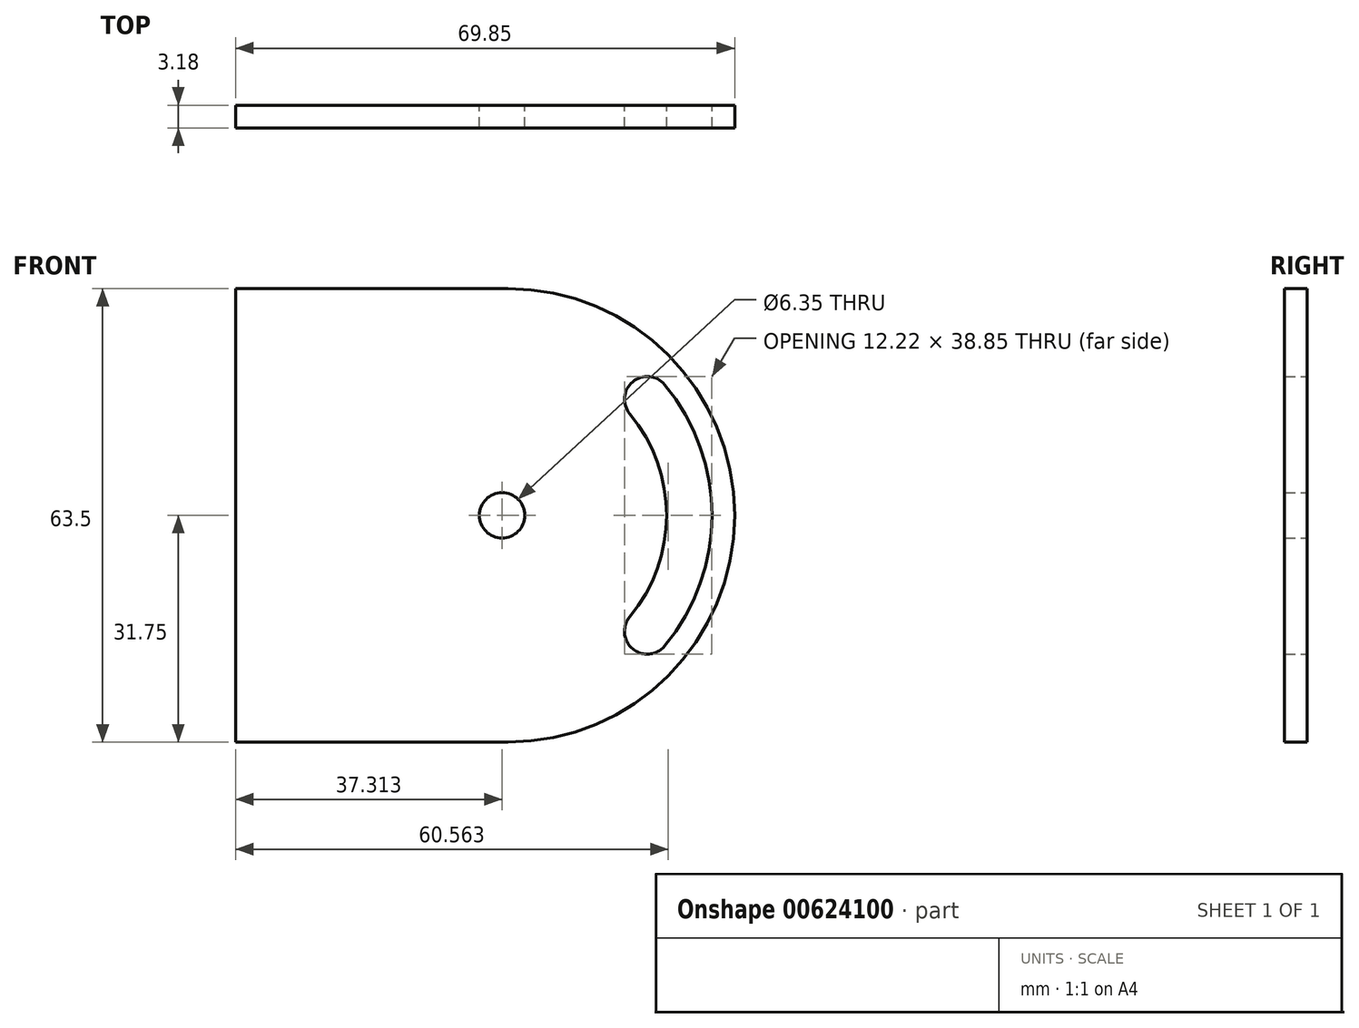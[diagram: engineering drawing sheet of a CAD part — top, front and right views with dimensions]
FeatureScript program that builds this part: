
annotation { "Feature Type Name" : "Feature", "Feature Type Description" : "" }
export const myFeature = defineFeature(function(context is Context, id is Id, definition is map)
    precondition{}
    {
        {
            var Q0;
            Q0=qCreatedBy(makeId("Front.planeOp"),FACE);
            var sketch = newSketch(context, id + "F0", { "sketchPlane" : qUnion([Q0])});
            skLineSegment(sketch, "E0.bottom", {"start": v(0, 0) * mm, "end": v(38.1, 0) * mm});
            skLineSegment(sketch, "E0.top", {"start": v(0, 63.5) * mm, "end": v(38.1, 63.5) * mm});
            skLineSegment(sketch, "E0.left", {"start": v(0, 0) * mm, "end": v(0, 63.5) * mm});
            skLineSegment(sketch, "E0.right", {"start": v(69.85, 31.75) * mm, "end": v(69.85, 31.75) * mm});
            skCircle(sketch, "E1", {"center": v(38.1, 31.75) * mm, "radius": 28.58 * mm});
            skCircle(sketch, "E2", {"center": v(38.1, 31.75) * mm, "radius": 22.23 * mm});
            skLineSegment(sketch, "E3", {"start": v(55.17, 45.98) * mm, "end": v(60.05, 50.04) * mm});
            skLineSegment(sketch, "E4", {"start": v(55.17, 17.52) * mm, "end": v(60.05, 13.46) * mm});
            skCircle(sketch, "E5", {"center": v(57.61, 15.49) * mm, "radius": 3.18 * mm});
            skCircle(sketch, "E6", {"center": v(57.61, 48.01) * mm, "radius": 3.18 * mm});
            skPoint(sketch, "E7.visualSharp", {"position": v(69.85, 63.5) * mm});
            skArc(sketch, "E7.filletArc", {"start": v(69.85, 31.75) * mm, "mid": v(60.55, 54.2) * mm, "end": v(38.1, 63.5) * mm});
            skPoint(sketch, "E8.visualSharp", {"position": v(69.85, 0) * mm});
            skArc(sketch, "E8.filletArc", {"start": v(38.1, 0) * mm, "mid": v(60.55, 9.3) * mm, "end": v(69.85, 31.75) * mm});
            skLineSegment(sketch, "E9", {"start": v(38.1, 31.75) * mm, "end": v(69.85, 31.75) * mm});
            skLineSegment(sketch, "E10", {"start": v(38.1, 31.75) * mm, "end": v(38.1, 31.75) * mm});
            skSolve(sketch);
        }
        {
            var Q0;
            {var subQ0=sQuery(id+"F0.wireOp",EDGE,"E6");var subQ1=sQuery(id+"F0.wireOp",EDGE,"E3");var subQ2=sQuery(id+"F0.wireOp",EDGE,"E1");var subQ3=makeQuery(id+"F0.imprint","INTERSECT",VERTEX,{"derivedFrom":[subQ2,subQ1,subQ0]});Q0=makeQuery(id+"F0.imprint","IMPRINT",FACE,{"disambiguationData":[TD([[makeQuery(id+"F0.imprint","IMPRINT",EDGE,{"disambiguationData":[TD([[subQ3,-1.0]])],"derivedFrom":subQ2}),1.0]])]});}
            var Q1;
            Q1=makeQuery(id+"F0.imprint","IMPRINT",FACE,{"disambiguationData":[TD([[makeQuery(id+"F0.imprint","IMPRINT",EDGE,{"derivedFrom":sQuery(id+"F0.wireOp",EDGE,"E0.bottom")}),1.0]])]});
            var Q2;
            Q2=makeQuery(id+"F0.imprint","IMPRINT",FACE,{"disambiguationData":[TD([[makeQuery(id+"F0.imprint","IMPRINT",EDGE,{"derivedFrom":sQuery(id+"F0.wireOp",EDGE,"WlHfUtpb-D6SS-SN8B-bFR3-Eu7baDn13T6m")}),-1.0]])]});
            var Q3;
            {var subQ0=sQuery(id+"F0.wireOp",EDGE,"E2");var subQ1=makeQuery(id+"F0.imprint","INTERSECT",VERTEX,{"derivedFrom":[subQ0,sQuery(id+"F0.wireOp",EDGE,"E3"),sQuery(id+"F0.wireOp",EDGE,"E6")]});Q3=makeQuery(id+"F0.imprint","IMPRINT",FACE,{"disambiguationData":[TD([[makeQuery(id+"F0.imprint","IMPRINT",EDGE,{"disambiguationData":[TD([[subQ1,-1.0]])],"derivedFrom":subQ0}),1.0]])]});}
            extrude(context, id + "F1", {"entities" : qUnion([Q0, Q1, Q2, Q3]), "depth" : 3.17 * mm, "offsetDistance" : 25.4 * mm});
        }
        {
            var Q0;
            Q0=makeQuery(id+"F1.opExtrude","CAP_FACE",FACE,{"disambiguationData":[OSD([sQuery(id+"F0.wireOp",EDGE,"E0.bottom"),sQuery(id+"F0.wireOp",EDGE,"E0.top"),sQuery(id+"F0.wireOp",EDGE,"E0.left"),sQuery(id+"F0.wireOp",EDGE,"WlHfUtpb-D6SS-SN8B-bFR3-Eu7baDn13T6m"),sQuery(id+"F0.wireOp",EDGE,"E1"),sQuery(id+"F0.wireOp",EDGE,"E2"),sQuery(id+"F0.wireOp",EDGE,"E5"),sQuery(id+"F0.wireOp",EDGE,"E6"),sQuery(id+"F0.wireOp",EDGE,"E7.filletArc"),sQuery(id+"F0.wireOp",EDGE,"E8.filletArc")])],"isStart":true});
            var sketch = newSketch(context, id + "F2", { "sketchPlane" : qUnion([Q0])});
            skLineSegment(sketch, "E11", {"start": v(-37.31, 31.75) * mm, "end": v(-60.33, 31.75) * mm});
            skCircle(sketch, "E12", {"center": v(-37.31, 31.75) * mm, "radius": 3.18 * mm});
            skSolve(sketch);
        }
        {
            var Q0;
            Q0=makeQuery(id+"F2.imprint","IMPRINT",FACE,{"disambiguationData":[TD([[makeQuery(id+"F2.imprint","IMPRINT",EDGE,{"derivedFrom":sQuery(id+"F2.wireOp",EDGE,"Qp62VUE4-ZY5p-XJ6P-mFSl-RnjpHC0UgmeZ")}),1.0]])]});
            var Q1;
            Q1=makeQuery(id+"F2.imprint","IMPRINT",FACE,{"disambiguationData":[TD([[makeQuery(id+"F2.imprint","IMPRINT",EDGE,{"derivedFrom":sQuery(id+"F2.wireOp",EDGE,"E12")}),1.0]])]});
            extrude(context, id + "F3", {"entities" : qUnion([Q0, Q1]), "operationType" : NewBodyOperationType.REMOVE, "oppositeDirection" : true, "depth" : 3.17 * mm, "offsetDistance" : 25.4 * mm});
        }
    });
